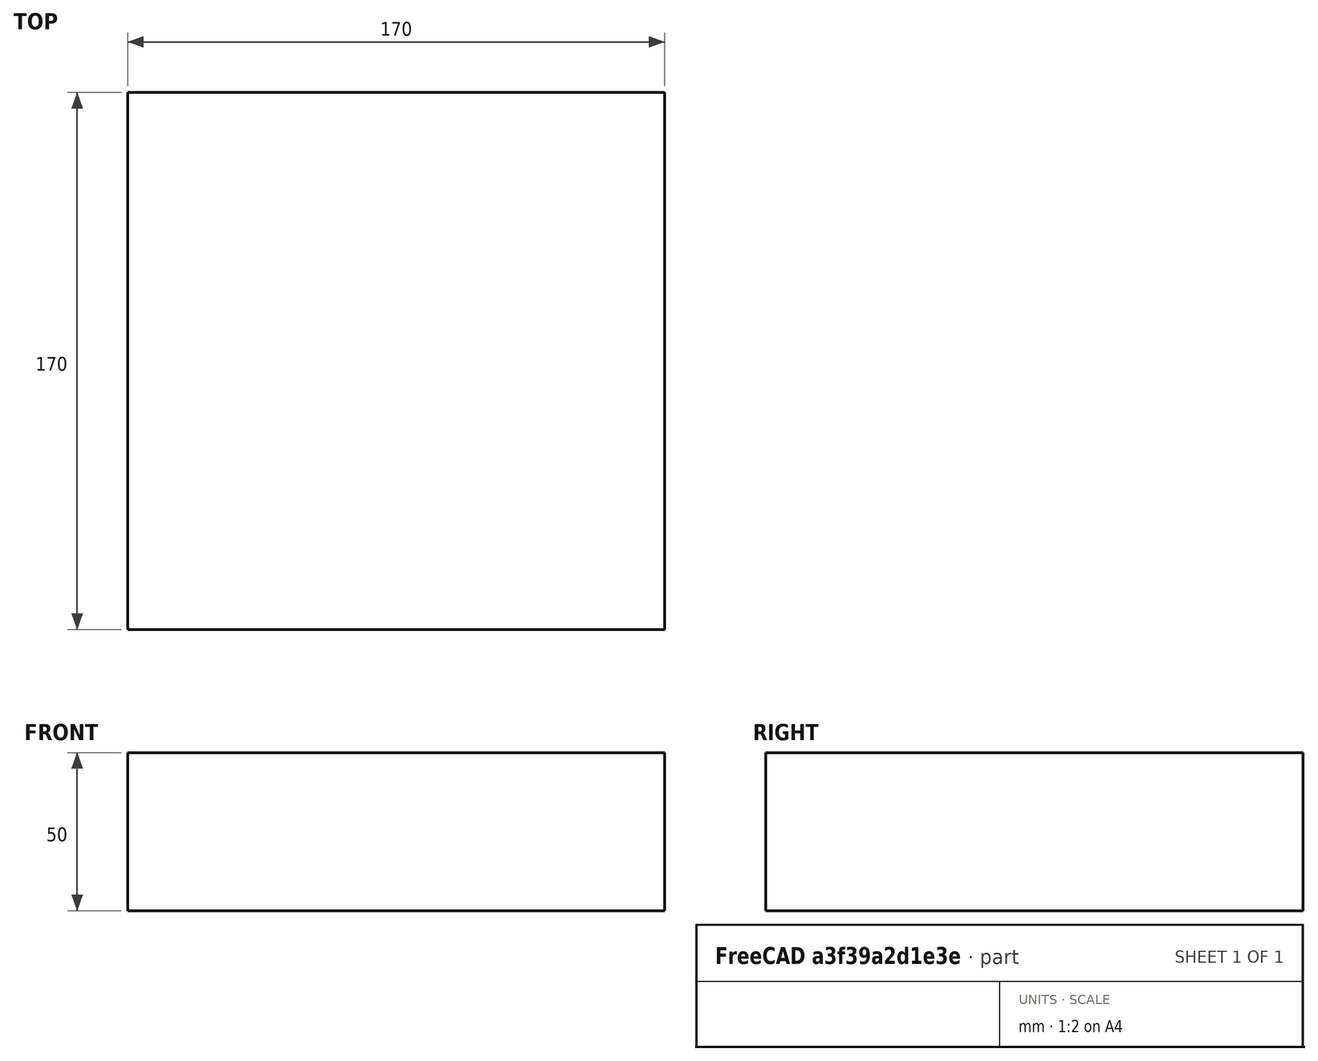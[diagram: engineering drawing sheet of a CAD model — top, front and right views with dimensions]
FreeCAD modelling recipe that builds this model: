
FCSTD DOCUMENT  (FreeCAD 0.15R4671 (Git))
Label: Square Bar 170 EN10059 S235JR
License: All rights reserved
LicenseURL: http://en.wikipedia.org/wiki/All_rights_reserved
objects: Sketcher::SketchObject×1, Part::Extrusion×1
note: 2 computed .brp shape members not serialized (recipe doc carries the construction recipe); baked Part::Feature solids carry a one-line shape summary decoded from their .brp

FEATURE [Sketcher::SketchObject] Sketch
  sketch-geometry (4):
    g0: LineSegment StartX=-85 StartY=-85 StartZ=0 EndX=85 EndY=-85 EndZ=0
    g1: LineSegment StartX=85 StartY=-85 StartZ=0 EndX=85 EndY=85 EndZ=0
    g2: LineSegment StartX=85 StartY=85 StartZ=0 EndX=-85 EndY=85 EndZ=0
    g3: LineSegment StartX=-85 StartY=85 StartZ=0 EndX=-85 EndY=-85 EndZ=0
  constraints (12):
    c: Coincident(g0,g1)
    c: Coincident(g1,g2)
    c: Coincident(g2,g3)
    c: Coincident(g3,g0)
    c: Horizontal(g0)
    c: Horizontal(g2)
    c: Vertical(g1)
    c: Vertical(g3)
    c: Symmetric(g1,g0,g-1)
    c: Symmetric(g2,g1,g-2)
    c: Equal(g1,g2)
    c: DistanceY(g1) = 170
FEATURE [Part::Extrusion] Extrude  label="Square Bar 170 EN10059 S235JR"
  Base = -> Sketch
  Dir = (0,0,50)
  Solid = true
